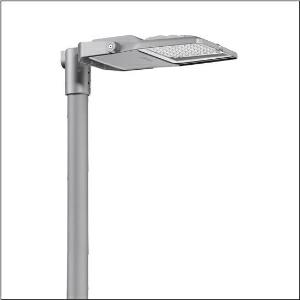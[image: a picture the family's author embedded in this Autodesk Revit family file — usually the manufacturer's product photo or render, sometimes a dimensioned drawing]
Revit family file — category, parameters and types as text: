
# Revit family: floodlight_fl_21_mini___pl52_5xa7776d2d3a_85e1
name_source: partatom
category: Lighting Fixtures
units: mm (PartAtom-declared; Revit-internal decimal feet)

## family parameters
Cut with Voids When Loaded = No
Host = Face
Light Source = No
Part Type = Normal
Room Calculation Point = No
Round Connector Dimension = Use Diameter
Shared = No

## types (1)
- --- (1 x LED, 17840 lm, 142.9 W, 3000K)
    Apparent Load = 143 VA
    CIE Flux Codes = 26 60 98 100 100
    Color Rendering = 70
    Color Temperature = 3000K
    Default Elevation = 1800 mm
    Description = Floodlight FL 21 mini, floodlight, primary light control with lens, of PMMA, primary optical cover: protective disc, of toughened safety glass, transparent, light distribution: PL52, light emission: direct distribution, installation type: surface-mounted, LED, High Power LED, rated luminous flux: 17.840lm, luminous efficacy: 125lm/W, light colour: 730, colour temperature: 3000K, control: flexible luminous flux parameterisation, time-dependent luminous flux control, constant luminous flux control, overheat protection, presetting dimming logarithmic, with terminal, 6-pole, mains connection: 220..240V, AC, 50/60Hz, start of lifetime: 143W, end of service life: 151W, reduction: 63W, luminaire housing, of diecast aluminium, powder-coated, Siteco® metallic grey (DB 702S), corrosivity category C5 mid according to DIN EN ISO 12944, sealing non-destructively replaceable, please order mast flange separately, mast bracket, of steel, galvanised, powder-coated, Siteco® metallic grey (DB 702S), Smart Interface below and above, protection rating (complete): IP66, insulation class (complete): insulation class II (safety insulation), certification: CE, ENEC, VDE, protection symbol: D, impact resistance: IK08, permissible operating ambient temperature: -40..+40°C, permissible operating ambient temperature for outdoor applications: -40..+50°C, standard: DIN EN 12944, LABS conformity tested according to VDMA 24364:2018-05, packaging unit: 1 piece

Light Distribution: PL52
    Height = 70 mm
    Lamp = 1 x LED
    Lamp Light Flux = 17840 lm
    Lamp Power = 142.9 W
    Lamp count = 1
    Length = 485 mm
    Luminous efficacy = 125 lm/W
    Manufacturer = Siteco
    ModVariant = No
    Model = 5XA7776D2D3A
    Number of Poles = 1
    OnlyDefault = Yes
    Power Factor = 1
    Product Name = Floodlight FL 21 mini | PL52
    Product group = floodlight | pylon annexe
    ProductGroupID = 6200
    Protection Class = Protection class II
    Protection Degree = IP 66
    RLX_Detail_Level = 1
    RLX_Emergency_Light_Flux = 0 lm
    RLX_Emergency_Type = 0
    RLX_Emergency_Type_DB = No
    RlxData = <blob elided: 101345 chars, md5=7092da85>
    Socket = socket
    Standby Power = 0 W
    System Light Flux = 17840 lm
    System Power = 143 W
    Type Comments = factory setting: luminous flux: 100 % | dim-lin: 254 | 730 mA
    Type Image = l_1007125.jpg
    URL = http://relux.com
    VarID = @adj_113265
    Voltage = 0 V
    Weight = 0.00 kg
    Width = 337 mm

## geometry (parser evidence)
native form markers: Blend x4, Sweep x15
no freeform markers — native parametric forms only
